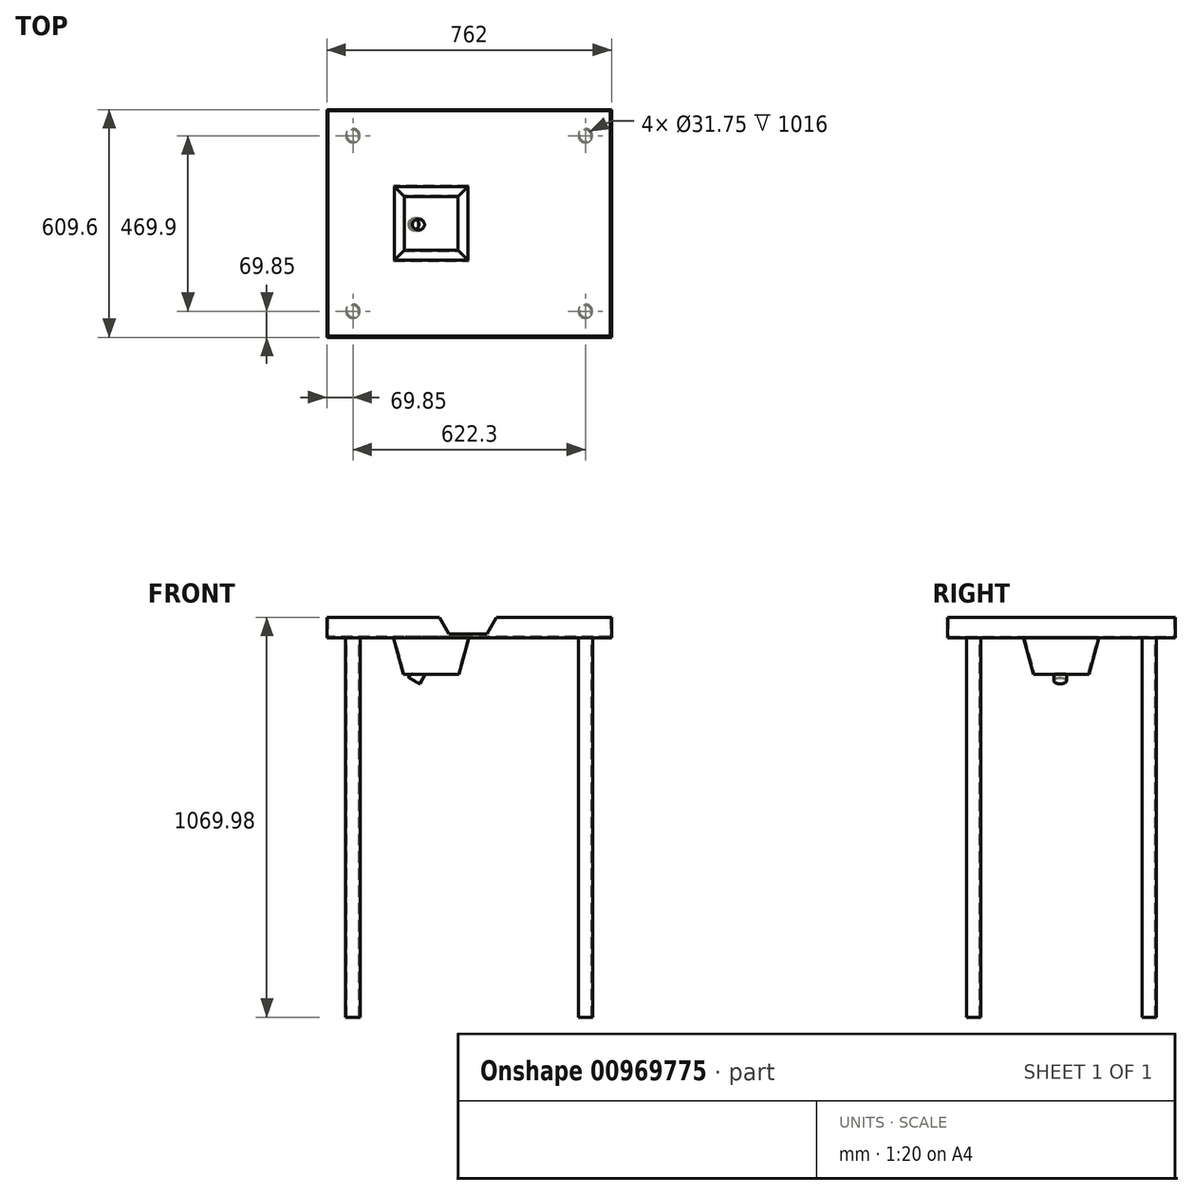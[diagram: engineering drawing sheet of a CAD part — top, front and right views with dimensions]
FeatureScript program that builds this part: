
annotation { "Feature Type Name" : "Feature", "Feature Type Description" : "" }
export const myFeature = defineFeature(function(context is Context, id is Id, definition is map)
    precondition{}
    {
        {
            var Q0;
            Q0=qCreatedBy(makeId("Top.planeOp"),FACE);
            var sketch = newSketch(context, id + "F0", { "sketchPlane" : qUnion([Q0])});
            skLineSegment(sketch, "E0.bottom", {"start": v(0, 0) * mm, "end": v(0, 0) * mm});
            skLineSegment(sketch, "E0.top", {"start": v(0, 0) * mm, "end": v(0, 0) * mm});
            skLineSegment(sketch, "E0.left", {"start": v(0, 0) * mm, "end": v(0, 0) * mm});
            skLineSegment(sketch, "E0.right", {"start": v(0, 0) * mm, "end": v(0, 0) * mm});
            skLineSegment(sketch, "E1.bottom", {"start": v(762, 609.6) * mm, "end": v(0, 609.6) * mm});
            skLineSegment(sketch, "E1.top", {"start": v(762, 0) * mm, "end": v(0, 0) * mm});
            skLineSegment(sketch, "E1.left", {"start": v(762, 609.6) * mm, "end": v(762, 0) * mm});
            skLineSegment(sketch, "E1.right", {"start": v(0, 609.6) * mm, "end": v(0, 0) * mm});
            skSolve(sketch);
        }
        {
            var Q0;
            Q0=makeQuery(id+"F0.imprint","IMPRINT",FACE,{"disambiguationData":[TD([[makeQuery(id+"F0.imprint","IMPRINT",EDGE,{"derivedFrom":sQuery(id+"F0.wireOp",EDGE,"E1.bottom")}),1.0]])]});
            extrude(context, id + "F1", {"entities" : qUnion([Q0]), "depth" : 3.17 * mm, "offsetDistance" : 25.4 * mm});
        }
        {
            var Q0;
            Q0=makeQuery(id+"F1.opExtrude","CAP_FACE",FACE,{"disambiguationData":[OSD([sQuery(id+"F0.wireOp",EDGE,"E1.bottom"),sQuery(id+"F0.wireOp",EDGE,"E1.top"),sQuery(id+"F0.wireOp",EDGE,"E1.left"),sQuery(id+"F0.wireOp",EDGE,"E1.right")])],"isStart":false});
            var sketch = newSketch(context, id + "F2", { "sketchPlane" : qUnion([Q0])});
            skLineSegment(sketch, "E2.bottom", {"start": v(0, 609.6) * mm, "end": v(762, 609.6) * mm});
            skLineSegment(sketch, "E2.top", {"start": v(0, 0) * mm, "end": v(762, 0) * mm});
            skLineSegment(sketch, "E2.left", {"start": v(0, 609.6) * mm, "end": v(0, 0) * mm});
            skLineSegment(sketch, "E2.right", {"start": v(762, 609.6) * mm, "end": v(762, 0) * mm});
            skLineSegment(sketch, "E3.bottom", {"start": v(758.82, 3.18) * mm, "end": v(3.18, 3.17) * mm});
            skLineSegment(sketch, "E3.top", {"start": v(758.82, 606.43) * mm, "end": v(3.17, 606.43) * mm});
            skLineSegment(sketch, "E3.left", {"start": v(758.82, 3.18) * mm, "end": v(758.82, 606.43) * mm});
            skLineSegment(sketch, "E3.right", {"start": v(3.17, 3.17) * mm, "end": v(3.17, 606.43) * mm});
            skSolve(sketch);
        }
        {
            var Q0;
            Q0=makeQuery(id+"F2.imprint","IMPRINT",FACE,{"disambiguationData":[TD([[makeQuery(id+"F2.imprint","IMPRINT",EDGE,{"derivedFrom":sQuery(id+"F2.wireOp",EDGE,"E2.bottom")}),1.0]])]});
            extrude(context, id + "F3", {"entities" : qUnion([Q0]), "operationType" : NewBodyOperationType.ADD, "depth" : 50.8 * mm, "offsetDistance" : 25.4 * mm});
        }
        {
            var Q0;
            Q0=makeQuery(id+"F3.boolean.opBoolean","MERGE",FACE,{"derivedFrom":[makeQuery(id+"F1.opExtrude","SWEPT_FACE",FACE,{"disambiguationData":[OSD([sQuery(id+"F0.wireOp",EDGE,"E1.top")])]}),makeQuery(id+"F3.opExtrude","SWEPT_FACE",FACE,{"disambiguationData":[OSD([sQuery(id+"F2.wireOp",EDGE,"E2.top")])]})]});
            var sketch = newSketch(context, id + "F4", { "sketchPlane" : qUnion([Q0])});
            skLineSegment(sketch, "E4", {"start": v(301.62, 53.98) * mm, "end": v(327.02, 9.53) * mm});
            skLineSegment(sketch, "E5", {"start": v(327.02, 9.52) * mm, "end": v(428.62, 9.52) * mm});
            skLineSegment(sketch, "E6", {"start": v(428.62, 9.52) * mm, "end": v(454.02, 53.98) * mm});
            skLineSegment(sketch, "E7", {"start": v(454.02, 53.97) * mm, "end": v(301.62, 53.97) * mm});
            skSolve(sketch);
        }
        {
            var Q0;
            Q0=makeQuery(id+"F4.imprint","IMPRINT",FACE,{"disambiguationData":[TD([[makeQuery(id+"F4.imprint","IMPRINT",EDGE,{"derivedFrom":sQuery(id+"F4.wireOp",EDGE,"E4")}),1.0]])]});
            extrude(context, id + "F5", {"entities" : qUnion([Q0]), "operationType" : NewBodyOperationType.REMOVE, "endBound" : BoundingType.THROUGH_ALL, "oppositeDirection" : true, "depth" : 25.4 * mm, "offsetDistance" : 25.4 * mm});
        }
        {
            var Q0;
            Q0=makeQuery(id+"F1.opExtrude","CAP_FACE",FACE,{"disambiguationData":[OSD([sQuery(id+"F0.wireOp",EDGE,"E1.bottom"),sQuery(id+"F0.wireOp",EDGE,"E1.top"),sQuery(id+"F0.wireOp",EDGE,"E1.left"),sQuery(id+"F0.wireOp",EDGE,"E1.right")])],"isStart":false});
            var sketch = newSketch(context, id + "F6", { "sketchPlane" : qUnion([Q0])});
            skLineSegment(sketch, "E8.bottom", {"start": v(381, 203.2) * mm, "end": v(177.8, 203.2) * mm});
            skLineSegment(sketch, "E8.top", {"start": v(381, 406.4) * mm, "end": v(177.8, 406.4) * mm});
            skLineSegment(sketch, "E8.left", {"start": v(381, 203.2) * mm, "end": v(381, 406.4) * mm});
            skLineSegment(sketch, "E8.right", {"start": v(177.8, 203.2) * mm, "end": v(177.8, 406.4) * mm});
            skSolve(sketch);
        }
        {
            var Q0;
            Q0=makeQuery(id+"F6.imprint","IMPRINT",FACE,{"disambiguationData":[TD([[makeQuery(id+"F6.imprint","IMPRINT",EDGE,{"derivedFrom":sQuery(id+"F6.wireOp",EDGE,"E8.bottom")}),-1.0]])]});
            extrude(context, id + "F7", {"entities" : qUnion([Q0]), "operationType" : NewBodyOperationType.ADD, "oppositeDirection" : true, "depth" : 101.6 * mm, "offsetDistance" : 25.4 * mm, "hasDraft" : true, "draftAngle" : 15 * degree, "draftPullDirection" : true});
        }
        {
            var Q0;
            Q0=makeQuery(id+"F7.opExtrude","CAP_EDGE",EDGE,{"disambiguationData":[OSD([sQuery(id+"F6.wireOp",EDGE,"E8.right")])],"isStart":false});
            cPlane(context, id + "F8", {"entities" : qUnion([Q0]), "cplaneType" : CPlaneType.LINE_ANGLE, "offset" : 25.4 * mm, "angle" : 30 * degree, "oppositeDirection" : true, "width" : 152.4 * mm, "height" : 152.4 * mm});
        }
        {
            var Q0;
            Q0=qCreatedBy(id+"F8.planeOp",FACE);
            var sketch = newSketch(context, id + "F9", { "sketchPlane" : qUnion([Q0])});
            skCircle(sketch, "E9", {"center": v(260.1, -301.86) * mm, "radius": 17.46 * mm});
            skSolve(sketch);
        }
        {
            var Q0;
            Q0=makeQuery(id+"F9.imprint","IMPRINT",FACE,{"disambiguationData":[TD([[makeQuery(id+"F9.imprint","IMPRINT",EDGE,{"derivedFrom":sQuery(id+"F9.wireOp",EDGE,"E9")}),1.0]])]});
            extrude(context, id + "F10", {"entities" : qUnion([Q0]), "operationType" : NewBodyOperationType.ADD, "endBound" : BoundingType.UP_TO_NEXT, "oppositeDirection" : true, "depth" : 25.4 * mm, "offsetDistance" : 25.4 * mm});
        }
        {
            var Q0;
            Q0=makeQuery(id+"F10.opExtrude","CAP_FACE",FACE,{"disambiguationData":[OSD([sQuery(id+"F9.wireOp",EDGE,"E9")])],"isStart":true});
            var Q1;
            Q1=makeQuery(id+"F1.opExtrude","CAP_FACE",FACE,{"disambiguationData":[OSD([sQuery(id+"F0.wireOp",EDGE,"E1.bottom"),sQuery(id+"F0.wireOp",EDGE,"E1.top"),sQuery(id+"F0.wireOp",EDGE,"E1.left"),sQuery(id+"F0.wireOp",EDGE,"E1.right")])],"isStart":false});
            shell(context, id + "F11", {"entities" : qUnion([Q0, Q1]), "thickness" : 3.17 * mm});
        }
        {
            var Q0;
            Q0=makeQuery(id+"F1.opExtrude","CAP_FACE",FACE,{"disambiguationData":[OSD([sQuery(id+"F0.wireOp",EDGE,"E1.bottom"),sQuery(id+"F0.wireOp",EDGE,"E1.top"),sQuery(id+"F0.wireOp",EDGE,"E1.left"),sQuery(id+"F0.wireOp",EDGE,"E1.right")])],"isStart":true});
            var sketch = newSketch(context, id + "F12", { "sketchPlane" : qUnion([Q0])});
            skCircle(sketch, "E10", {"center": v(69.85, -69.85) * mm, "radius": 19.05 * mm});
            skCircle(sketch, "E11", {"center": v(692.15, -69.85) * mm, "radius": 19.05 * mm});
            skCircle(sketch, "E12", {"center": v(692.15, -539.75) * mm, "radius": 19.05 * mm});
            skCircle(sketch, "E13", {"center": v(69.85, -539.75) * mm, "radius": 19.05 * mm});
            skSolve(sketch);
        }
        {
            var Q0;
            Q0 = qSketchRegion(id + "F12", true);
            extrude(context, id + "F13", {"entities" : qUnion([Q0]), "operationType" : NewBodyOperationType.ADD, "depth" : 1016 * mm, "offsetDistance" : 25.4 * mm});
        }
        {
            var Q0;
            Q0=makeQuery(id+"F13.opExtrude","CAP_FACE",FACE,{"disambiguationData":[OSD([sQuery(id+"F12.wireOp",EDGE,"E10")])],"isStart":false});
            var Q1;
            Q1=makeQuery(id+"F13.opExtrude","CAP_FACE",FACE,{"disambiguationData":[OSD([sQuery(id+"F12.wireOp",EDGE,"E13")])],"isStart":false});
            var Q2;
            Q2=makeQuery(id+"F13.opExtrude","CAP_FACE",FACE,{"disambiguationData":[OSD([sQuery(id+"F12.wireOp",EDGE,"E12")])],"isStart":false});
            var Q3;
            Q3=makeQuery(id+"F13.opExtrude","CAP_FACE",FACE,{"disambiguationData":[OSD([sQuery(id+"F12.wireOp",EDGE,"E11")])],"isStart":false});
            shell(context, id + "F14", {"entities" : qUnion([Q0, Q1, Q2, Q3]), "thickness" : 3.17 * mm});
        }
    });
